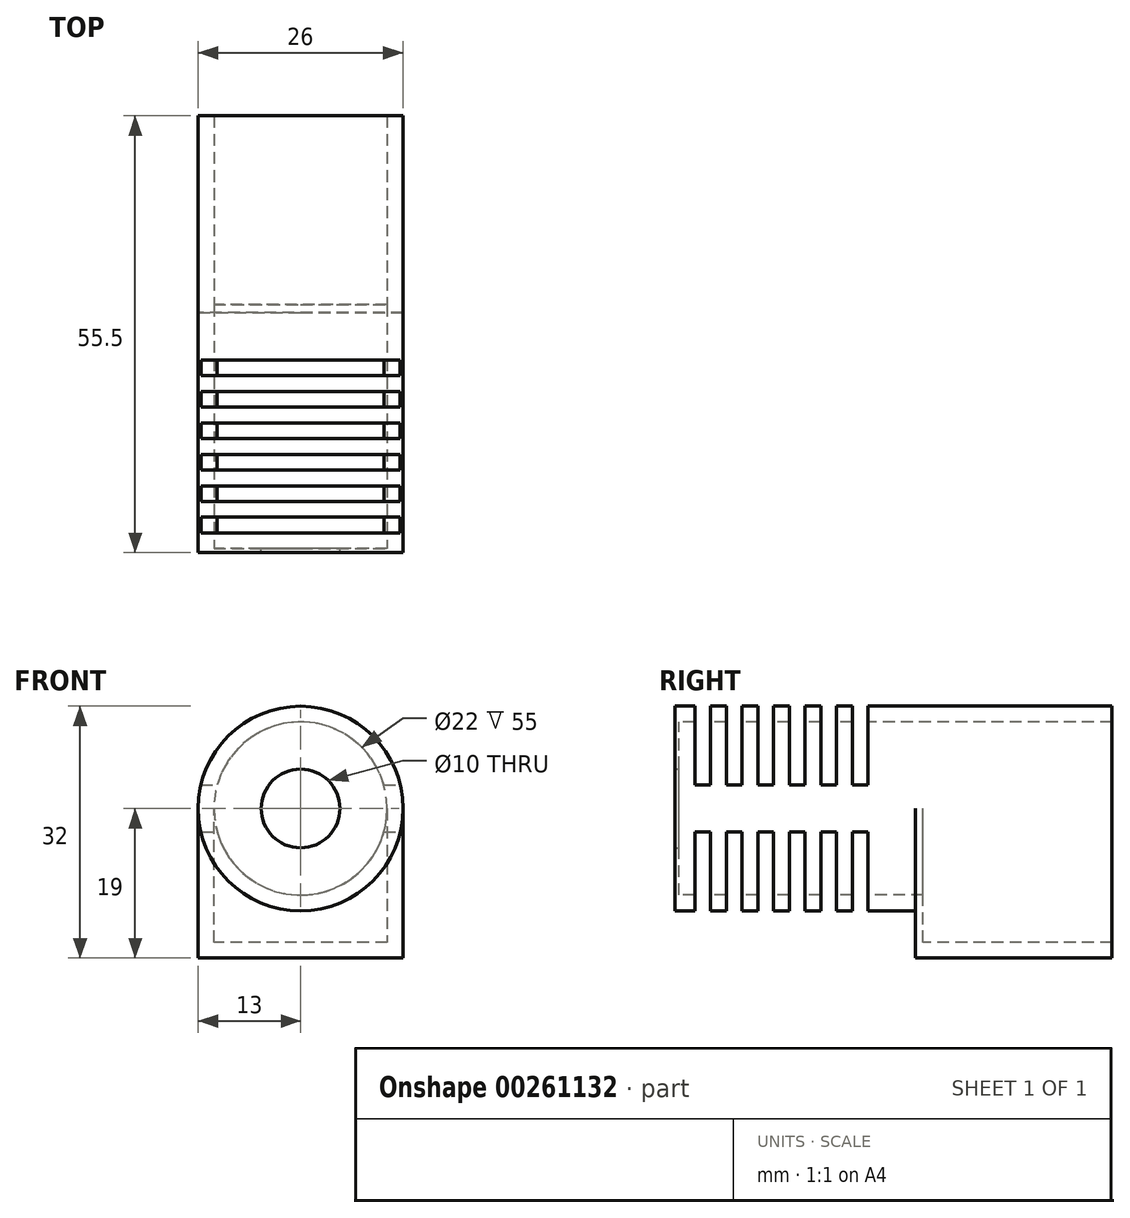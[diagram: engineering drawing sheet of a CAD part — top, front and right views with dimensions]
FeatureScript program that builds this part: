
annotation { "Feature Type Name" : "Feature", "Feature Type Description" : "" }
export const myFeature = defineFeature(function(context is Context, id is Id, definition is map)
    precondition{}
    {
        {
            var Q0;
            Q0=qCreatedBy(makeId("Front.planeOp"),FACE);
            var sketch = newSketch(context, id + "F0", { "sketchPlane" : qUnion([Q0])});
            skCircle(sketch, "E0", {"center": v(0, 0) * mm, "radius": 13 * mm});
            skCircle(sketch, "E1", {"center": v(0, 0) * mm, "radius": 11 * mm});
            skSolve(sketch);
        }
        {
            var Q0;
            Q0=qSketchRegion(id+"F0",true);
            extrude(context, id + "F1", {"entities" : qUnion([Q0]), "oppositeDirection" : true, "depth" : 30 * mm});
        }
        {
            var Q0;
            Q0=qCreatedBy(makeId("Front.planeOp"),FACE);
            var sketch = newSketch(context, id + "F2", { "sketchPlane" : qUnion([Q0])});
            skCircle(sketch, "E2", {"center": v(0, 0) * mm, "radius": 13 * mm});
            skCircle(sketch, "E3", {"center": v(0, 0) * mm, "radius": 5 * mm});
            skSolve(sketch);
        }
        {
            var Q0;
            Q0=qSketchRegion(id+"F2",true);
            extrude(context, id + "F3", {"entities" : qUnion([Q0]), "operationType" : NewBodyOperationType.ADD, "depth" : 0.5 * mm});
        }
        {
            var Q0;
            Q0=qCreatedBy(makeId("Top.planeOp"),FACE);
            cPlane(context, id + "F4", {"entities" : qUnion([Q0]), "cplaneType" : CPlaneType.OFFSET, "offset" : 13 * mm, "width" : 150 * mm, "height" : 150 * mm});
        }
        {
            var Q0;
            Q0=qCreatedBy(id+"F4.planeOp",FACE);
            var sketch = newSketch(context, id + "F5", { "sketchPlane" : qUnion([Q0])});
            skLineSegment(sketch, "E4", {"start": v(-13, 0) * mm, "end": v(13, 0) * mm});
            skLineSegment(sketch, "E5", {"start": v(-13, 2) * mm, "end": v(-13, 4) * mm});
            skLineSegment(sketch, "E6", {"start": v(-13, 26) * mm, "end": v(13, 26) * mm});
            skLineSegment(sketch, "E7", {"start": v(13, 24) * mm, "end": v(13, 22) * mm});
            skLineSegment(sketch, "E8.0.1.0", {"start": v(-13, 2) * mm, "end": v(13, 2) * mm});
            skLineSegment(sketch, "E8.0.2.0", {"start": v(-13, 4) * mm, "end": v(13, 4) * mm});
            skLineSegment(sketch, "E8.0.3.0", {"start": v(-13, 6) * mm, "end": v(13, 6) * mm});
            skLineSegment(sketch, "E8.0.4.0", {"start": v(-13, 8) * mm, "end": v(13, 8) * mm});
            skLineSegment(sketch, "E8.0.5.0", {"start": v(-13, 10) * mm, "end": v(13, 10) * mm});
            skLineSegment(sketch, "E8.0.6.0", {"start": v(-13, 12) * mm, "end": v(13, 12) * mm});
            skLineSegment(sketch, "E8.0.7.0", {"start": v(-13, 14) * mm, "end": v(13, 14) * mm});
            skLineSegment(sketch, "E8.0.8.0", {"start": v(-13, 16) * mm, "end": v(13, 16) * mm});
            skLineSegment(sketch, "E8.0.9.0", {"start": v(-13, 18) * mm, "end": v(13, 18) * mm});
            skLineSegment(sketch, "E8.0.10.0", {"start": v(-13, 20) * mm, "end": v(13, 20) * mm});
            skLineSegment(sketch, "E8.0.11.0", {"start": v(-13, 22) * mm, "end": v(13, 22) * mm});
            skLineSegment(sketch, "E8.0.12.0", {"start": v(-13, 24) * mm, "end": v(13, 24) * mm});
            skLineSegment(sketch, "E9.trimOffspring", {"start": v(-13, 22) * mm, "end": v(-13, 24) * mm});
            skLineSegment(sketch, "E10.trimOffspring", {"start": v(13, 20) * mm, "end": v(13, 18) * mm});
            skLineSegment(sketch, "E11.trimOffspring", {"start": v(-13, 18) * mm, "end": v(-13, 20) * mm});
            skLineSegment(sketch, "E12.trimOffspring", {"start": v(13, 16) * mm, "end": v(13, 14) * mm});
            skLineSegment(sketch, "E13.trimOffspring", {"start": v(-13, 14) * mm, "end": v(-13, 16) * mm});
            skLineSegment(sketch, "E14.trimOffspring", {"start": v(13, 12) * mm, "end": v(13, 10) * mm});
            skLineSegment(sketch, "E15.trimOffspring", {"start": v(-13, 10) * mm, "end": v(-13, 12) * mm});
            skLineSegment(sketch, "E16.trimOffspring", {"start": v(13, 8) * mm, "end": v(13, 6) * mm});
            skLineSegment(sketch, "E17.trimOffspring", {"start": v(-13, 6) * mm, "end": v(-13, 8) * mm});
            skLineSegment(sketch, "E18.trimOffspring", {"start": v(13, 4) * mm, "end": v(13, 2) * mm});
            skLineSegment(sketch, "E19", {"start": v(0, -4) * mm, "end": v(0, -5) * mm});
            skSolve(sketch);
        }
        {
            var Q0;
            Q0=qSketchRegion(id+"F5",true);
            extrude(context, id + "F6", {"entities" : qUnion([Q0]), "operationType" : NewBodyOperationType.REMOVE, "oppositeDirection" : true, "depth" : 10 * mm});
        }
        {
            var Q0;
            Q0=qCreatedBy(makeId("Top.planeOp"),FACE);
            cPlane(context, id + "F7", {"entities" : qUnion([Q0]), "cplaneType" : CPlaneType.OFFSET, "offset" : 13 * mm, "oppositeDirection" : true, "width" : 150 * mm, "height" : 150 * mm});
        }
        {
            var Q0;
            Q0=qCreatedBy(id+"F7.planeOp",FACE);
            var sketch = newSketch(context, id + "F8", { "sketchPlane" : qUnion([Q0])});
            skLineSegment(sketch, "E20", {"start": v(13, 2) * mm, "end": v(13, 4) * mm});
            skLineSegment(sketch, "E21", {"start": v(-13, 2) * mm, "end": v(-13, 4) * mm});
            skLineSegment(sketch, "E22.0.1.0", {"start": v(-13, 2) * mm, "end": v(13, 2) * mm});
            skLineSegment(sketch, "E22.0.2.0", {"start": v(-13, 4) * mm, "end": v(13, 4) * mm});
            skLineSegment(sketch, "E22.0.3.0", {"start": v(-13, 6) * mm, "end": v(13, 6) * mm});
            skLineSegment(sketch, "E22.0.4.0", {"start": v(-13, 8) * mm, "end": v(13, 8) * mm});
            skLineSegment(sketch, "E22.0.5.0", {"start": v(-13, 10) * mm, "end": v(13, 10) * mm});
            skLineSegment(sketch, "E22.0.6.0", {"start": v(-13, 12) * mm, "end": v(13, 12) * mm});
            skLineSegment(sketch, "E22.0.7.0", {"start": v(-13, 14) * mm, "end": v(13, 14) * mm});
            skLineSegment(sketch, "E22.0.8.0", {"start": v(-13, 16) * mm, "end": v(13, 16) * mm});
            skLineSegment(sketch, "E22.0.9.0", {"start": v(-13, 18) * mm, "end": v(13, 18) * mm});
            skLineSegment(sketch, "E22.0.10.0", {"start": v(-13, 20) * mm, "end": v(13, 20) * mm});
            skLineSegment(sketch, "E22.0.11.0", {"start": v(-13, 22) * mm, "end": v(13, 22) * mm});
            skLineSegment(sketch, "E22.0.12.0", {"start": v(-13, 24) * mm, "end": v(13, 24) * mm});
            skLineSegment(sketch, "E23.trimOffspring", {"start": v(-13, 6) * mm, "end": v(-13, 8) * mm});
            skLineSegment(sketch, "E24.trimOffspring", {"start": v(13, 6) * mm, "end": v(13, 8) * mm});
            skLineSegment(sketch, "E25.trimOffspring", {"start": v(-13, 4) * mm, "end": v(-13, 2) * mm});
            skLineSegment(sketch, "E26.trimOffspring", {"start": v(-13, 8) * mm, "end": v(-13, 6) * mm});
            skLineSegment(sketch, "E27.trimOffspring", {"start": v(-13, 10) * mm, "end": v(-13, 12) * mm});
            skLineSegment(sketch, "E28.trimOffspring", {"start": v(13, 10) * mm, "end": v(13, 12) * mm});
            skLineSegment(sketch, "E29.trimOffspring", {"start": v(-13, 12) * mm, "end": v(-13, 10) * mm});
            skLineSegment(sketch, "E30.trimOffspring", {"start": v(-13, 14) * mm, "end": v(-13, 16) * mm});
            skLineSegment(sketch, "E31.trimOffspring", {"start": v(13, 14) * mm, "end": v(13, 16) * mm});
            skLineSegment(sketch, "E32.trimOffspring", {"start": v(-13, 16) * mm, "end": v(-13, 14) * mm});
            skLineSegment(sketch, "E33.trimOffspring", {"start": v(13, 18) * mm, "end": v(13, 20) * mm});
            skLineSegment(sketch, "E34.trimOffspring", {"start": v(-13, 20) * mm, "end": v(-13, 18) * mm});
            skLineSegment(sketch, "E35.trimOffspring", {"start": v(-13, 22) * mm, "end": v(-13, 24) * mm});
            skLineSegment(sketch, "E36.trimOffspring", {"start": v(13, 22) * mm, "end": v(13, 24) * mm});
            skLineSegment(sketch, "E37.trimOffspring", {"start": v(-13, 24) * mm, "end": v(-13, 22) * mm});
            skSolve(sketch);
        }
        {
            var Q0;
            Q0=qSketchRegion(id+"F8",true);
            extrude(context, id + "F9", {"entities" : qUnion([Q0]), "operationType" : NewBodyOperationType.REMOVE, "depth" : 10 * mm});
        }
        {
            var Q0;
            Q0=makeQuery(id+"F1.opExtrude","CAP_FACE",FACE,{"disambiguationData":[OSD([sQuery(id+"F0.wireOp",EDGE,"E0"),sQuery(id+"F0.wireOp",EDGE,"E1")])],"isStart":false});
            var sketch = newSketch(context, id + "F10", { "sketchPlane" : qUnion([Q0])});
            skArc(sketch, "E38", {"start": v(11, -6.93) * mm, "mid": v(0, 13) * mm, "end": v(-11, -6.93) * mm});
            skLineSegment(sketch, "E39", {"start": v(-13, 0) * mm, "end": v(-13, -19) * mm});
            skLineSegment(sketch, "E40", {"start": v(-13, -19) * mm, "end": v(13, -19) * mm});
            skLineSegment(sketch, "E41", {"start": v(13, -19) * mm, "end": v(13, 0) * mm});
            skLineSegment(sketch, "E42", {"start": v(-11, 0) * mm, "end": v(-11, -17) * mm});
            skLineSegment(sketch, "E43", {"start": v(-11, -17) * mm, "end": v(11, -17) * mm});
            skLineSegment(sketch, "E44", {"start": v(11, -17) * mm, "end": v(11, 0) * mm});
            skSolve(sketch);
        }
        {
            var Q0;
            {var subQ0=sQuery(id+"F10.wireOp",EDGE,"E38");var subQ1=makeQuery(id+"F10.imprint","INTERSECT",VERTEX,{"derivedFrom":[subQ0,sQuery(id+"F10.wireOp",EDGE,"E39")]});Q0=makeQuery(id+"F10.imprint","IMPRINT",FACE,{"disambiguationData":[TD([[makeQuery(id+"F10.imprint","IMPRINT",EDGE,{"disambiguationData":[TD([[subQ1,-1.0]])],"derivedFrom":subQ0}),-1.0]])]});}
            var Q1;
            {var subQ0=sQuery(id+"F10.wireOp",EDGE,"E39");Q1=makeQuery(id+"F10.imprint","IMPRINT",FACE,{"disambiguationData":[TD([[makeQuery(id+"F10.imprint","IMPRINT",EDGE,{"derivedFrom":subQ0}),1.0]])]});}
            extrude(context, id + "F11", {"entities" : qUnion([Q0, Q1]), "operationType" : NewBodyOperationType.ADD, "depth" : 25 * mm});
        }
        {
            var Q0;
            Q0=makeQuery(id+"F1.opExtrude","CAP_FACE",FACE,{"disambiguationData":[OSD([sQuery(id+"F0.wireOp",EDGE,"E0"),sQuery(id+"F0.wireOp",EDGE,"E1")])],"isStart":false});
            var sketch = newSketch(context, id + "F12", { "sketchPlane" : qUnion([Q0])});
            skCircle(sketch, "E45", {"center": v(0, 0) * mm, "radius": 13 * mm});
            skLineSegment(sketch, "E46", {"start": v(-13, 0) * mm, "end": v(-13, -19) * mm});
            skLineSegment(sketch, "E47", {"start": v(-13, -19) * mm, "end": v(13, -19) * mm});
            skLineSegment(sketch, "E48", {"start": v(13, -19) * mm, "end": v(13, 0) * mm});
            skSolve(sketch);
        }
        {
            var Q0;
            {var subQ0=sQuery(id+"F12.wireOp",EDGE,"E46");Q0=makeQuery(id+"F12.imprint","IMPRINT",FACE,{"disambiguationData":[TD([[makeQuery(id+"F12.imprint","IMPRINT",EDGE,{"derivedFrom":subQ0}),1.0]])]});}
            var Q1;
            {var subQ1=sQuery(id+"F0.wireOp",EDGE,"E1");Q1=makeQuery(id+"F12.imprint","IMPRINT",FACE,{"disambiguationData":[TD([[makeQuery(id+"F12.imprint","IMPRINT",EDGE,{"derivedFrom":makeQuery(id+"F1.opExtrude","CAP_EDGE",EDGE,{"disambiguationData":[OSD([subQ1])],"isStart":false})}),1.0]])]});}
            extrude(context, id + "F13", {"entities" : qUnion([Q0, Q1]), "operationType" : NewBodyOperationType.ADD, "depth" : 1 * mm});
        }
    });
